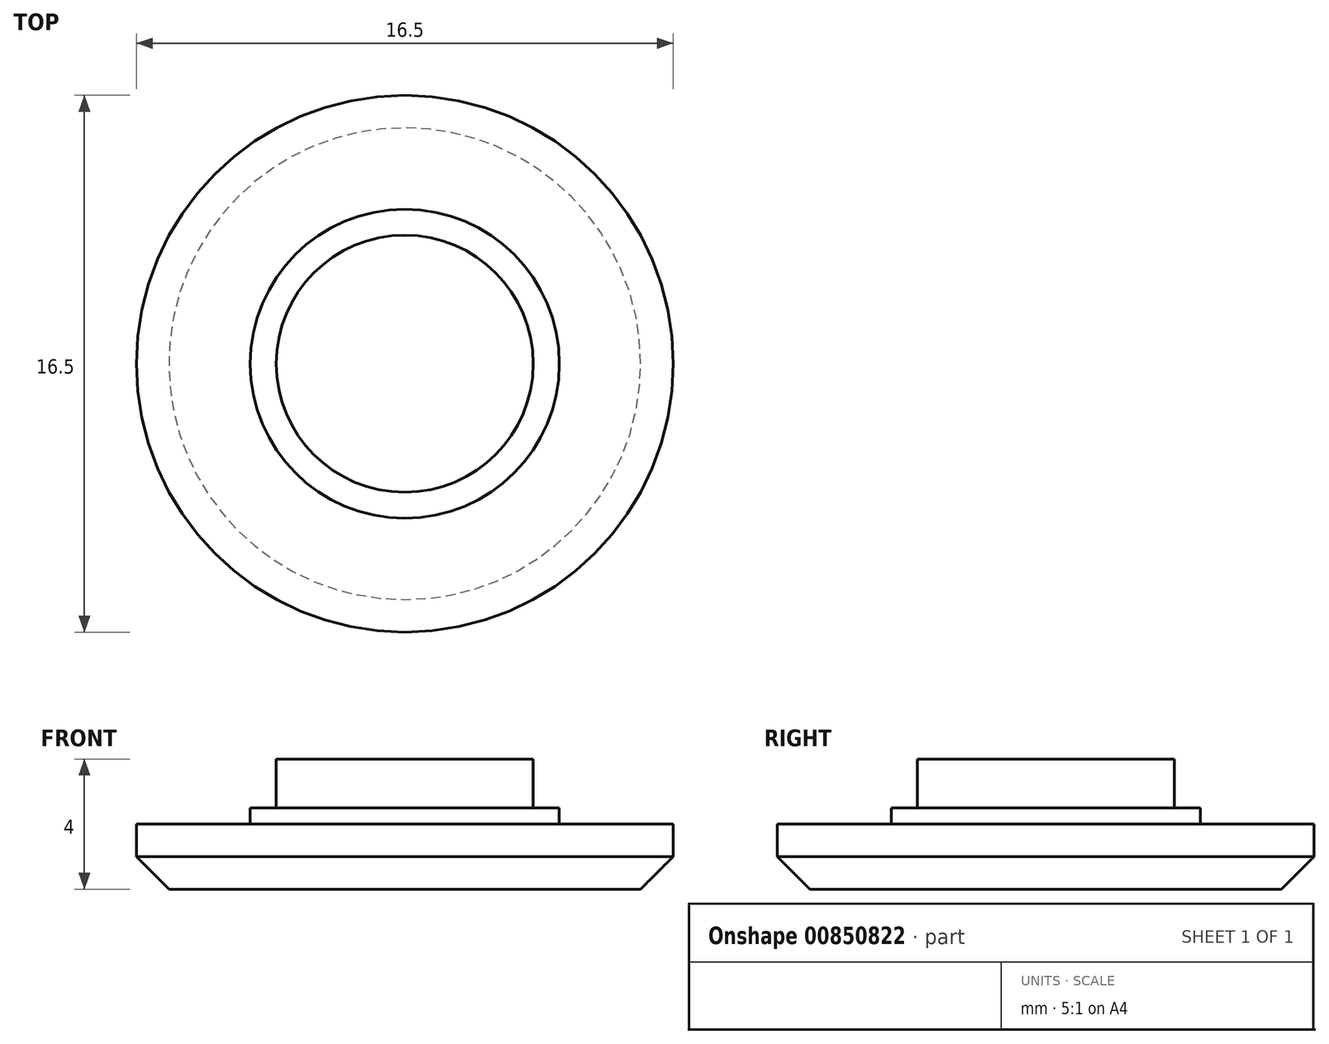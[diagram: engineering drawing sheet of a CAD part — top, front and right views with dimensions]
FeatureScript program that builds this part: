
annotation { "Feature Type Name" : "Feature", "Feature Type Description" : "" }
export const myFeature = defineFeature(function(context is Context, id is Id, definition is map)
    precondition{}
    {
        {
            var Q0;
            Q0=qCreatedBy(makeId("Top.planeOp"),FACE);
            var sketch = newSketch(context, id + "F0", { "sketchPlane" : qUnion([Q0])});
            skCircle(sketch, "E0", {"center": v(0, 0) * mm, "radius": 3.95 * mm});
            skCircle(sketch, "E1", {"center": v(0, 0) * mm, "radius": 4.75 * mm});
            skCircle(sketch, "E2", {"center": v(0, 0) * mm, "radius": 8.25 * mm});
            skSolve(sketch);
        }
        {
            var Q0;
            Q0=makeQuery(id+"F0.imprint","IMPRINT",FACE,{"disambiguationData":[TD([[makeQuery(id+"F0.imprint","IMPRINT",EDGE,{"derivedFrom":sQuery(id+"F0.wireOp",EDGE,"E0")}),1.0]])]});
            extrude(context, id + "F1", {"entities" : qUnion([Q0]), "depth" : 2 * mm, "offsetDistance" : 25 * mm});
        }
        {
            var Q0;
            Q0=makeQuery(id+"F0.imprint","IMPRINT",FACE,{"disambiguationData":[TD([[makeQuery(id+"F0.imprint","IMPRINT",EDGE,{"derivedFrom":sQuery(id+"F0.wireOp",EDGE,"E1")}),-1.0]])]});
            var Q1;
            Q1=makeQuery(id+"F0.imprint","IMPRINT",FACE,{"disambiguationData":[TD([[makeQuery(id+"F0.imprint","IMPRINT",EDGE,{"derivedFrom":sQuery(id+"F0.wireOp",EDGE,"E0")}),1.0]])]});
            var Q2;
            Q2=makeQuery(id+"F0.imprint","IMPRINT",FACE,{"disambiguationData":[TD([[makeQuery(id+"F0.imprint","IMPRINT",EDGE,{"derivedFrom":sQuery(id+"F0.wireOp",EDGE,"E0")}),-1.0]])]});
            extrude(context, id + "F2", {"entities" : qUnion([Q0, Q1, Q2]), "oppositeDirection" : true, "depth" : 2 * mm, "offsetDistance" : 25 * mm});
        }
        {
            var Q0;
            Q0=makeQuery(id+"F0.imprint","IMPRINT",FACE,{"disambiguationData":[TD([[makeQuery(id+"F0.imprint","IMPRINT",EDGE,{"derivedFrom":sQuery(id+"F0.wireOp",EDGE,"E0")}),-1.0]])]});
            var Q1;
            Q1=makeQuery(id+"F0.imprint","IMPRINT",FACE,{"disambiguationData":[TD([[makeQuery(id+"F0.imprint","IMPRINT",EDGE,{"derivedFrom":sQuery(id+"F0.wireOp",EDGE,"E0")}),1.0]])]});
            extrude(context, id + "F3", {"entities" : qUnion([Q0, Q1]), "operationType" : NewBodyOperationType.ADD, "depth" : 0.5 * mm, "offsetDistance" : 25 * mm});
        }
        {
            var Q0;
            Q0=makeQuery(id+"F2.opExtrude","CAP_EDGE",EDGE,{"disambiguationData":[OSD([sQuery(id+"F0.wireOp",EDGE,"E2")])],"isStart":false});
            chamfer(context, id + "F4", {"entities" : qUnion([Q0]), "width" : 1 * mm, "tangentPropagation" : true});
        }
    });
